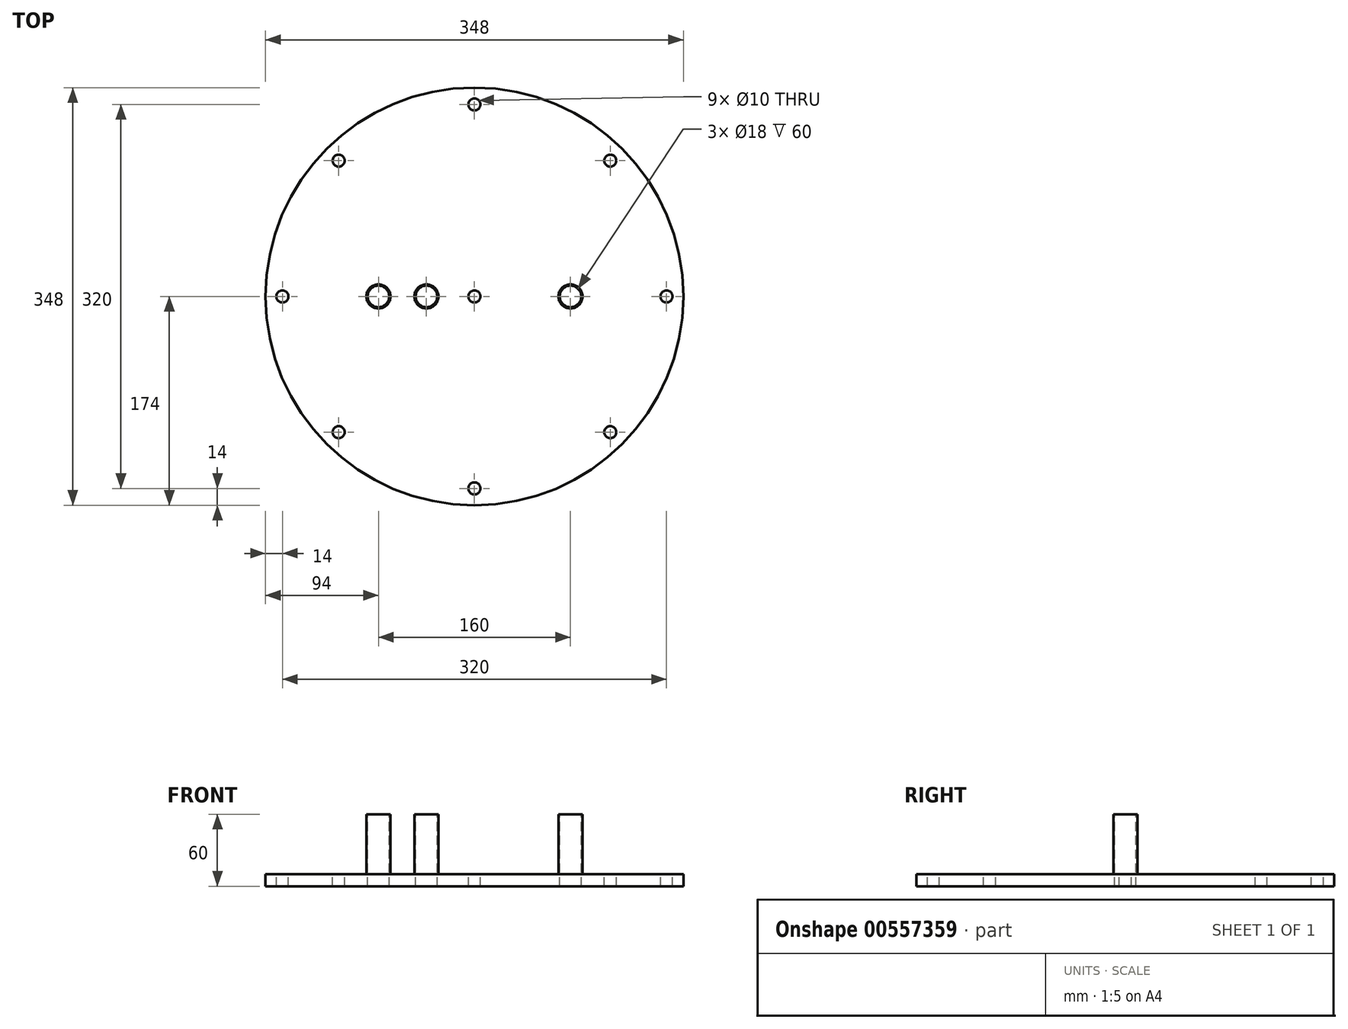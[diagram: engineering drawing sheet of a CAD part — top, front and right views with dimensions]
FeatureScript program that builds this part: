
annotation { "Feature Type Name" : "Feature", "Feature Type Description" : "" }
export const myFeature = defineFeature(function(context is Context, id is Id, definition is map)
    precondition{}
    {
        {
            var Q0;
            Q0=qCreatedBy(makeId("Top.planeOp"),FACE);
            var sketch = newSketch(context, id + "F0", { "sketchPlane" : qUnion([Q0])});
            skCircle(sketch, "E0", {"center": v(0, 0) * mm, "radius": 174 * mm});
            skSolve(sketch);
        }
        {
            var Q0;
            Q0 = qSketchRegion(id + "F0", true);
            extrude(context, id + "F1", {"entities" : qUnion([Q0]), "depth" : 10 * mm, "offsetDistance" : 25 * mm});
        }
        {
            var Q0;
            Q0=makeQuery(id+"F1.opExtrude","CAP_FACE",FACE,{"disambiguationData":[OSD([sQuery(id+"F0.wireOp",EDGE,"E0")])],"isStart":false});
            var sketch = newSketch(context, id + "F2", { "sketchPlane" : qUnion([Q0])});
            skCircle(sketch, "E1", {"center": v(0, 160) * mm, "radius": 5 * mm});
            skCircle(sketch, "E2.1.0", {"center": v(-113.14, 113.14) * mm, "radius": 5 * mm});
            skCircle(sketch, "E2.2.0", {"center": v(-160, 0) * mm, "radius": 5 * mm});
            skPoint(sketch, "E2.center", {"position": v(0, 0) * mm});
            skCircle(sketch, "E3.1.3.0", {"center": v(-113.14, -113.14) * mm, "radius": 5 * mm});
            skCircle(sketch, "E3.1.4.0", {"center": v(0, -160) * mm, "radius": 5 * mm});
            skCircle(sketch, "E3.1.5.0", {"center": v(113.14, -113.14) * mm, "radius": 5 * mm});
            skCircle(sketch, "E3.1.6.0", {"center": v(160, 0) * mm, "radius": 5 * mm});
            skCircle(sketch, "E3.1.7.0", {"center": v(113.14, 113.14) * mm, "radius": 5 * mm});
            skSolve(sketch);
        }
        {
            var Q0;
            Q0 = qSketchRegion(id + "F2", true);
            var Q1;
            Q1=makeQuery(id+"F1.opExtrude","CAP_FACE",FACE,{"disambiguationData":[OSD([sQuery(id+"F0.wireOp",EDGE,"E0")])],"isStart":true});
            extrude(context, id + "F3", {"entities" : qUnion([Q0]), "operationType" : NewBodyOperationType.REMOVE, "endBound" : BoundingType.UP_TO_SURFACE, "oppositeDirection" : true, "depth" : 25 * mm, "endBoundEntityFace" : qUnion([Q1]), "offsetDistance" : 25 * mm});
        }
        {
            var Q0;
            Q0=makeQuery(id+"F1.opExtrude","CAP_FACE",FACE,{"disambiguationData":[OSD([sQuery(id+"F0.wireOp",EDGE,"E0")])],"isStart":false});
            var sketch = newSketch(context, id + "F4", { "sketchPlane" : qUnion([Q0])});
            skCircle(sketch, "E4", {"center": v(0, 0) * mm, "radius": 5 * mm});
            skSolve(sketch);
        }
        {
            var Q0;
            Q0=makeQuery(id+"F4.imprint","IMPRINT",FACE,{"disambiguationData":[TD([[makeQuery(id+"F4.imprint","IMPRINT",EDGE,{"derivedFrom":sQuery(id+"F4.wireOp",EDGE,"E4")}),1.0]])]});
            var Q1;
            Q1=makeQuery(id+"F1.opExtrude","CAP_FACE",FACE,{"disambiguationData":[OSD([sQuery(id+"F0.wireOp",EDGE,"E0")])],"isStart":true});
            extrude(context, id + "F5", {"entities" : qUnion([Q0]), "operationType" : NewBodyOperationType.REMOVE, "endBound" : BoundingType.UP_TO_SURFACE, "oppositeDirection" : true, "depth" : 25 * mm, "endBoundEntityFace" : qUnion([Q1]), "offsetDistance" : 25 * mm});
        }
        {
            var Q0;
            Q0=makeQuery(id+"F1.opExtrude","CAP_FACE",FACE,{"disambiguationData":[OSD([sQuery(id+"F0.wireOp",EDGE,"E0")])],"isStart":false});
            var sketch = newSketch(context, id + "F6", { "sketchPlane" : qUnion([Q0])});
            skCircle(sketch, "E5", {"center": v(-80, 0) * mm, "radius": 10 * mm});
            skCircle(sketch, "E6", {"center": v(-40, 0) * mm, "radius": 10 * mm});
            skCircle(sketch, "E7", {"center": v(80, 0) * mm, "radius": 10 * mm});
            skSolve(sketch);
        }
        {
            var Q0;
            Q0=makeQuery(id+"F6.imprint","IMPRINT",FACE,{"disambiguationData":[TD([[makeQuery(id+"F6.imprint","IMPRINT",EDGE,{"derivedFrom":sQuery(id+"F6.wireOp",EDGE,"E7")}),1.0]])]});
            var Q1;
            Q1=makeQuery(id+"F6.imprint","IMPRINT",FACE,{"disambiguationData":[TD([[makeQuery(id+"F6.imprint","IMPRINT",EDGE,{"derivedFrom":sQuery(id+"F6.wireOp",EDGE,"E6")}),1.0]])]});
            var Q2;
            Q2=makeQuery(id+"F6.imprint","IMPRINT",FACE,{"disambiguationData":[TD([[makeQuery(id+"F6.imprint","IMPRINT",EDGE,{"derivedFrom":sQuery(id+"F6.wireOp",EDGE,"E5")}),1.0]])]});
            extrude(context, id + "F7", {"entities" : qUnion([Q0, Q1, Q2]), "operationType" : NewBodyOperationType.ADD, "depth" : 50 * mm, "offsetDistance" : 25 * mm});
        }
        {
            var Q0;
            Q0=makeQuery(id+"F7.opExtrude","CAP_FACE",FACE,{"disambiguationData":[OSD([sQuery(id+"F6.wireOp",EDGE,"E6")])],"isStart":false});
            var sketch = newSketch(context, id + "F8", { "sketchPlane" : qUnion([Q0])});
            skCircle(sketch, "E8", {"center": v(-40, 0) * mm, "radius": 9 * mm});
            skSolve(sketch);
        }
        {
            var Q0;
            Q0=makeQuery(id+"F7.opExtrude","CAP_FACE",FACE,{"disambiguationData":[OSD([sQuery(id+"F6.wireOp",EDGE,"E5")])],"isStart":false});
            var sketch = newSketch(context, id + "F9", { "sketchPlane" : qUnion([Q0])});
            skCircle(sketch, "E9", {"center": v(-80, 0) * mm, "radius": 9 * mm});
            skSolve(sketch);
        }
        {
            var Q0;
            Q0=makeQuery(id+"F7.opExtrude","CAP_FACE",FACE,{"disambiguationData":[OSD([sQuery(id+"F6.wireOp",EDGE,"E7")])],"isStart":false});
            var sketch = newSketch(context, id + "F10", { "sketchPlane" : qUnion([Q0])});
            skCircle(sketch, "E10", {"center": v(80, 0) * mm, "radius": 9 * mm});
            skSolve(sketch);
        }
        {
            var Q0;
            Q0=makeQuery(id+"F9.imprint","IMPRINT",FACE,{"disambiguationData":[TD([[makeQuery(id+"F9.imprint","IMPRINT",EDGE,{"derivedFrom":sQuery(id+"F9.wireOp",EDGE,"E9")}),1.0]])]});
            var Q1;
            Q1=makeQuery(id+"F8.imprint","IMPRINT",FACE,{"disambiguationData":[TD([[makeQuery(id+"F8.imprint","IMPRINT",EDGE,{"derivedFrom":sQuery(id+"F8.wireOp",EDGE,"E8")}),1.0]])]});
            var Q2;
            Q2=makeQuery(id+"F10.imprint","IMPRINT",FACE,{"disambiguationData":[TD([[makeQuery(id+"F10.imprint","IMPRINT",EDGE,{"derivedFrom":sQuery(id+"F10.wireOp",EDGE,"E10")}),1.0]])]});
            var Q3;
            Q3=makeQuery(id+"F1.opExtrude","CAP_FACE",FACE,{"disambiguationData":[OSD([sQuery(id+"F0.wireOp",EDGE,"E0")])],"isStart":true});
            extrude(context, id + "F11", {"entities" : qUnion([Q0, Q1, Q2]), "operationType" : NewBodyOperationType.REMOVE, "endBound" : BoundingType.UP_TO_SURFACE, "oppositeDirection" : true, "depth" : 25 * mm, "endBoundEntityFace" : qUnion([Q3]), "offsetDistance" : 25 * mm});
        }
    });
